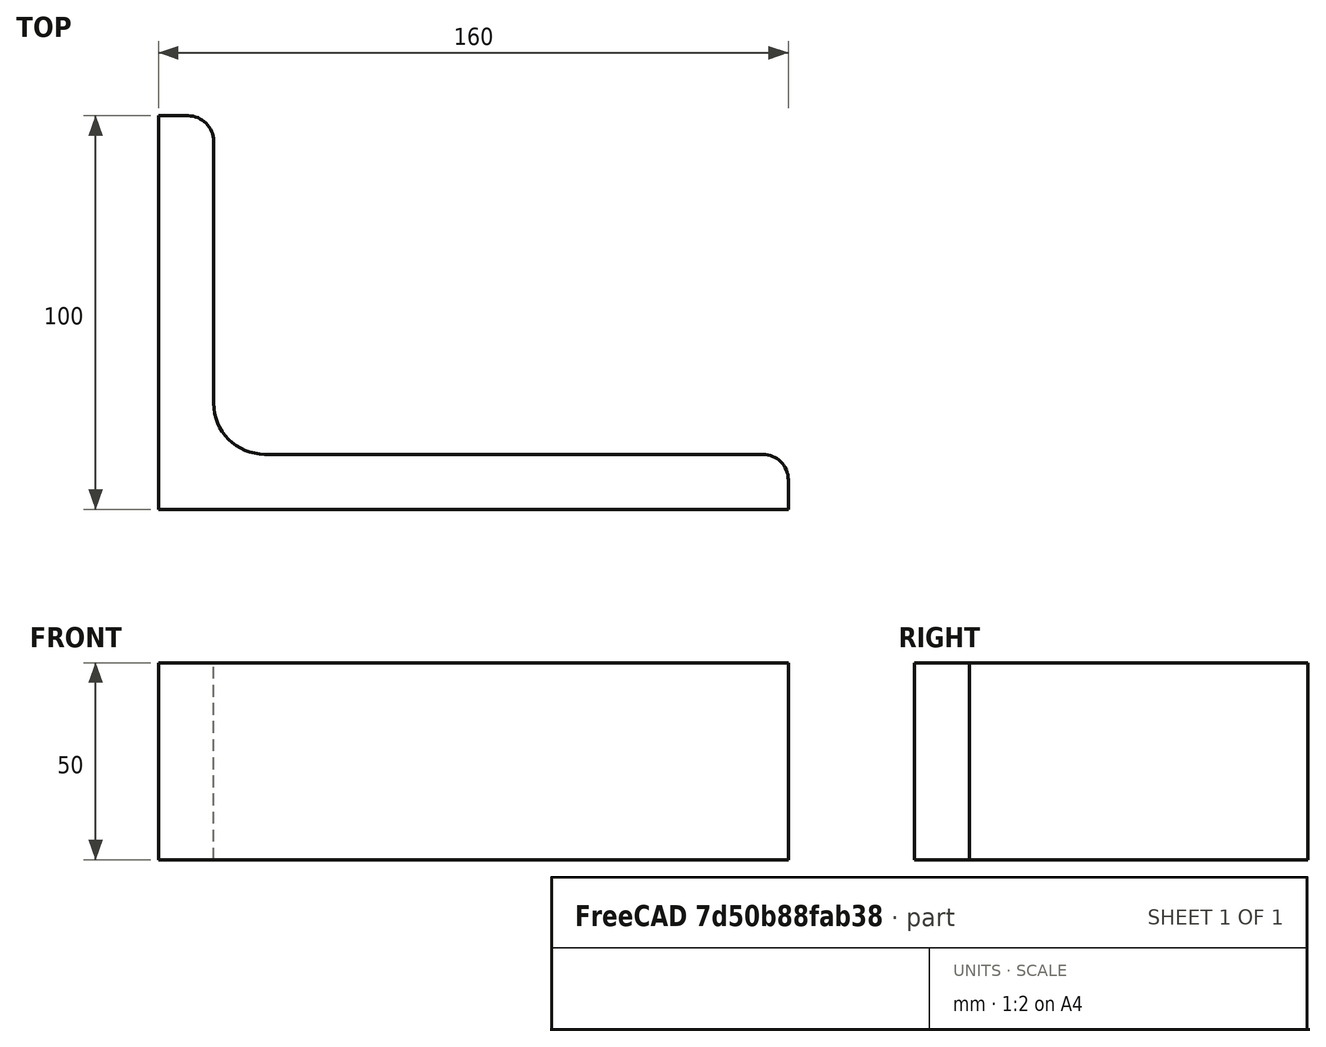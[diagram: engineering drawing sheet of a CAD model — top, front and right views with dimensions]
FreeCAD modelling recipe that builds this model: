
FCSTD DOCUMENT  (FreeCAD 0.15R4671 (Git))
Label: Angle Bar 160x100x14 EN10056 S235JR
License: All rights reserved
LicenseURL: http://en.wikipedia.org/wiki/All_rights_reserved
objects: Sketcher::SketchObject×1, Part::Extrusion×1
note: 2 computed .brp shape members not serialized (recipe doc carries the construction recipe); baked Part::Feature solids carry a one-line shape summary decoded from their .brp

FEATURE [Sketcher::SketchObject] Sketch
  sketch-geometry (9):
    g0: LineSegment StartX=0 StartY=0 StartZ=0 EndX=160 EndY=0 EndZ=0
    g1: LineSegment StartX=160 StartY=0 StartZ=0 EndX=160 EndY=7.5 EndZ=0
    g2: LineSegment StartX=153.5 StartY=14 StartZ=0 EndX=27 EndY=14 EndZ=0
    g3: LineSegment StartX=0 StartY=0 StartZ=0 EndX=0 EndY=100 EndZ=0
    g4: LineSegment StartX=0 StartY=100 StartZ=0 EndX=7.5 EndY=100 EndZ=0
    g5: LineSegment StartX=14 StartY=93.5 StartZ=0 EndX=14 EndY=27 EndZ=0
    g6: ArcOfCircle CenterX=27 CenterY=27 CenterZ=0 NormalX=0 NormalY=0 NormalZ=1 Radius=13 StartAngle=3.14159 EndAngle=4.71239
    g7: ArcOfCircle CenterX=7.5 CenterY=93.5 CenterZ=0 NormalX=0 NormalY=0 NormalZ=1 Radius=6.5 StartAngle=0 EndAngle=1.5708
    g8: ArcOfCircle CenterX=153.5 CenterY=7.5 CenterZ=0 NormalX=0 NormalY=0 NormalZ=1 Radius=6.5 StartAngle=0 EndAngle=1.5708
  constraints (23):
    c: Coincident(g0,g-1)
    c: Horizontal(g0)
    c: Coincident(g1,g0)
    c: Vertical(g1)
    c: Horizontal(g2)
    c: Coincident(g3,g-1)
    c: Vertical(g3)
    c: Coincident(g4,g3)
    c: Horizontal(g4)
    c: Vertical(g5)
    c: Tangent(g5,g6) = -1.5708
    c: Tangent(g2,g6) = 1.5708
    c: Tangent(g4,g7) = 1.5708
    c: Tangent(g5,g7) = 1.5708
    c: Tangent(g2,g8) = -1.5708
    c: Tangent(g1,g8) = -1.5708
    c: DistanceX(g0) = 160
    c: DistanceY(g3) = 100
    c: DistanceY(g0,g2) = 14
    c: DistanceX(g3,g5) = 14
    c: Radius(g6) = 13
    c: Radius(g8) = 6.5
    c: Radius(g7) = 6.5
FEATURE [Part::Extrusion] Extrude  label="Angle Bar 160x100x14 EN10056 S235JR"
  Base = -> Sketch
  Dir = (0,0,50)
  Solid = true
